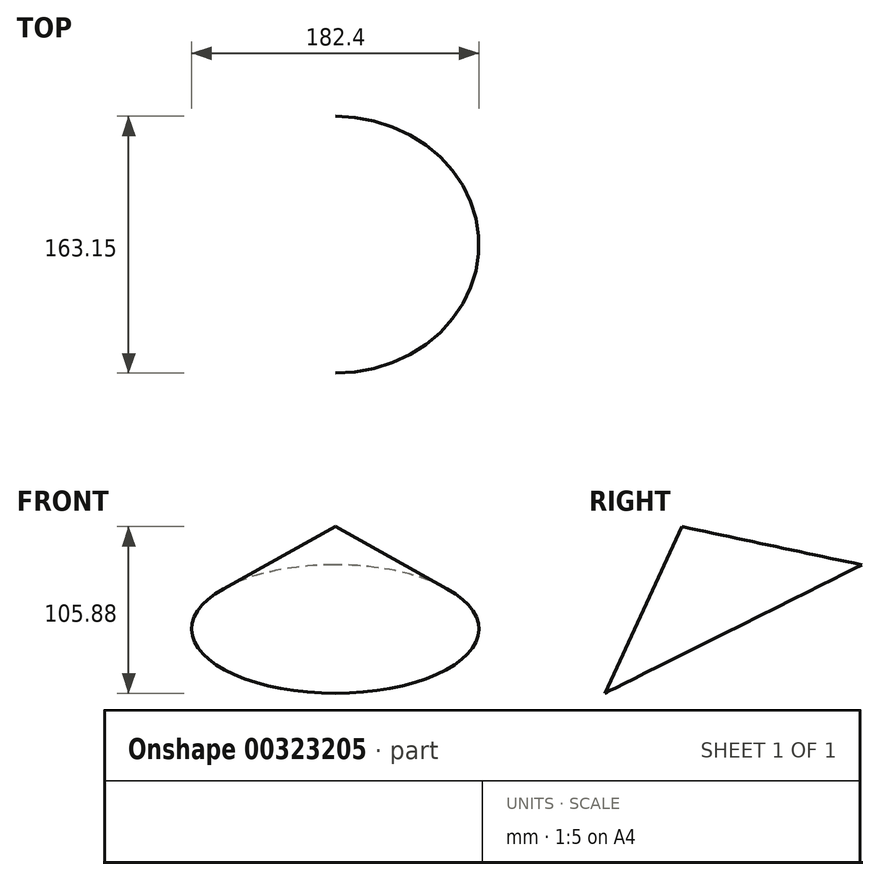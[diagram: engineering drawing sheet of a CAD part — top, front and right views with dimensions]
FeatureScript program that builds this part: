
annotation { "Feature Type Name" : "Feature", "Feature Type Description" : "" }
export const myFeature = defineFeature(function(context is Context, id is Id, definition is map)
    precondition{}
    {
        {
            var Q0;
            Q0=qCreatedBy(makeId("Right.planeOp"),FACE);
            var sketch = newSketch(context, id + "F0", { "sketchPlane" : qUnion([Q0])});
            skLineSegment(sketch, "E0", {"start": v(52.34, -75.2) * mm, "end": v(0, 29.48) * mm});
            skLineSegment(sketch, "E1", {"start": v(0, 29.48) * mm, "end": v(-49.03, -76.4) * mm});
            skSolve(sketch);
        }
        {
            var Q0;
            Q0=sQuery(id+"F0.wireOp",EDGE,"E1");
            var Q1;
            Q1=sQuery(id+"F0.wireOp",EDGE,"E0");
            revolve(context, id + "F1", {"bodyType" : ToolBodyType.SURFACE, "surfaceEntities" : qUnion([Q0]), "axis" : qUnion([Q1]), "revolveType" : RevolveType.FULL});
        }
    });
